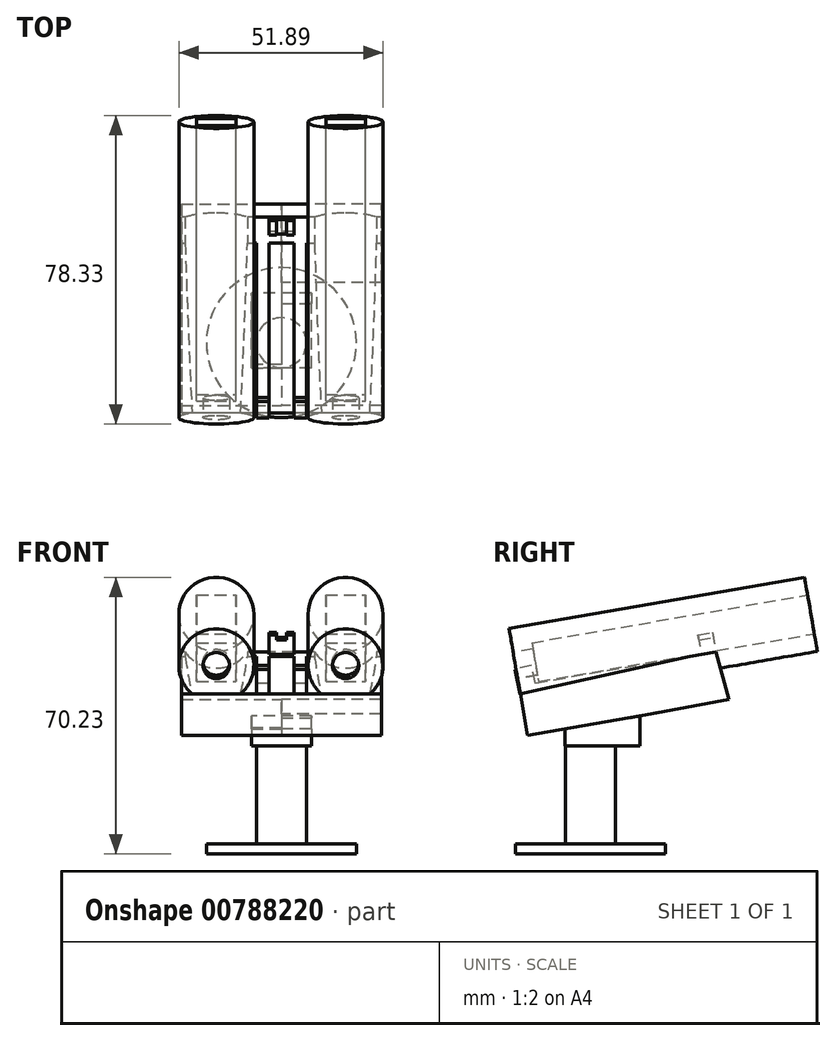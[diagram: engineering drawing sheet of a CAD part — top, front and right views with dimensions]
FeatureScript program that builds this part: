
annotation { "Feature Type Name" : "Feature", "Feature Type Description" : "" }
export const myFeature = defineFeature(function(context is Context, id is Id, definition is map)
    precondition{}
    {
        {
            var Q0;
            Q0=qCreatedBy(makeId("Top.planeOp"),FACE);
            var sketch = newSketch(context, id + "F0", { "sketchPlane" : qUnion([Q0])});
            skCircle(sketch, "E0", {"center": v(0, 0) * mm, "radius": 19.05 * mm});
            skSolve(sketch);
        }
        {
            var Q0;
            Q0 = qSketchRegion(id + "F0", true);
            extrude(context, id + "F1", {"entities" : qUnion([Q0]), "depth" : 2.54 * mm, "offsetDistance" : 25.4 * mm});
        }
        {
            var Q0;
            Q0=makeQuery(id+"F1.opExtrude","CAP_FACE",FACE,{"disambiguationData":[OSD([sQuery(id+"F0.wireOp",EDGE,"E0")])],"isStart":false});
            var sketch = newSketch(context, id + "F2", { "sketchPlane" : qUnion([Q0])});
            skCircle(sketch, "E1", {"center": v(0, 0) * mm, "radius": 6.35 * mm});
            skSolve(sketch);
        }
        {
            var Q0;
            Q0 = qSketchRegion(id + "F2", true);
            extrude(context, id + "F3", {"entities" : qUnion([Q0]), "operationType" : NewBodyOperationType.ADD, "depth" : 25.4 * mm, "offsetDistance" : 25.4 * mm});
        }
        {
            var Q0;
            Q0=qCreatedBy(makeId("Right.planeOp"),FACE);
            var sketch = newSketch(context, id + "F4", { "sketchPlane" : qUnion([Q0])});
            skLineSegment(sketch, "E2", {"start": v(-6.4, 27.4) * mm, "end": v(12.65, 27.4) * mm});
            skLineSegment(sketch, "E3", {"start": v(12.65, 27.4) * mm, "end": v(12.65, 35.02) * mm});
            skLineSegment(sketch, "E4", {"start": v(12.65, 35.02) * mm, "end": v(-6.4, 31.8) * mm});
            skLineSegment(sketch, "E5", {"start": v(-6.4, 31.8) * mm, "end": v(-6.4, 27.4) * mm});
            skSolve(sketch);
        }
        {
            var Q0;
            Q0 = qSketchRegion(id + "F4", true);
            extrude(context, id + "F5", {"entities" : qUnion([Q0]), "operationType" : NewBodyOperationType.ADD, "depth" : 7.62 * mm, "offsetDistance" : 25.4 * mm});
        }
        {
            var Q0;
            Q0=makeQuery(id+"F5.opExtrude","CAP_FACE",FACE,{"disambiguationData":[OSD([sQuery(id+"F4.wireOp",EDGE,"E2"),sQuery(id+"F4.wireOp",EDGE,"E3"),sQuery(id+"F4.wireOp",EDGE,"E4"),sQuery(id+"F4.wireOp",EDGE,"E5")])],"isStart":true});
            var sketch = newSketch(context, id + "F6", { "sketchPlane" : qUnion([Q0])});
            skLineSegment(sketch, "E6", {"start": v(-12.65, 27.4) * mm, "end": v(6.4, 27.4) * mm});
            skLineSegment(sketch, "E7", {"start": v(6.4, 27.4) * mm, "end": v(6.4, 31.8) * mm});
            skLineSegment(sketch, "E8", {"start": v(6.4, 31.8) * mm, "end": v(-12.65, 35.02) * mm});
            skLineSegment(sketch, "E9", {"start": v(-12.65, 35.02) * mm, "end": v(-12.65, 27.4) * mm});
            skSolve(sketch);
        }
        {
            var Q0;
            Q0 = qSketchRegion(id + "F6", true);
            extrude(context, id + "F7", {"entities" : qUnion([Q0]), "operationType" : NewBodyOperationType.ADD, "depth" : 7.62 * mm, "offsetDistance" : 25.4 * mm});
        }
        {
            var Q0;
            Q0=qCreatedBy(makeId("Right.planeOp"),FACE);
            var sketch = newSketch(context, id + "F8", { "sketchPlane" : qUnion([Q0])});
            skLineSegment(sketch, "E10", {"start": v(15.34, 35.5) * mm, "end": v(-15.94, 30.08) * mm});
            skLineSegment(sketch, "E11", {"start": v(-15.94, 30.08) * mm, "end": v(-18.11, 42.59) * mm});
            skLineSegment(sketch, "E12", {"start": v(-18.11, 42.59) * mm, "end": v(31.94, 51.26) * mm});
            skLineSegment(sketch, "E13", {"start": v(15.34, 35.5) * mm, "end": v(35.23, 39.24) * mm});
            skLineSegment(sketch, "E14", {"start": v(35.23, 39.24) * mm, "end": v(31.94, 51.26) * mm});
            skSolve(sketch);
        }
        {
            var Q0;
            Q0 = qSketchRegion(id + "F8", true);
            extrude(context, id + "F9", {"entities" : qUnion([Q0]), "operationType" : NewBodyOperationType.ADD, "depth" : 25.4 * mm, "offsetDistance" : 25.4 * mm});
        }
        {
            var Q0;
            Q0=makeQuery(id+"F9.opExtrude","CAP_FACE",FACE,{"disambiguationData":[OSD([sQuery(id+"F8.wireOp",EDGE,"E10"),sQuery(id+"F8.wireOp",EDGE,"E11"),sQuery(id+"F8.wireOp",EDGE,"E12"),sQuery(id+"F8.wireOp",EDGE,"E13"),sQuery(id+"F8.wireOp",EDGE,"E14")])],"isStart":true});
            var sketch = newSketch(context, id + "F10", { "sketchPlane" : qUnion([Q0])});
            skLineSegment(sketch, "E15", {"start": v(-35.23, 39.24) * mm, "end": v(15.94, 30.08) * mm});
            skLineSegment(sketch, "E16", {"start": v(15.94, 30.08) * mm, "end": v(18.11, 42.59) * mm});
            skLineSegment(sketch, "E17", {"start": v(18.11, 42.59) * mm, "end": v(-31.94, 51.26) * mm});
            skLineSegment(sketch, "E18", {"start": v(-31.94, 51.26) * mm, "end": v(-35.23, 39.24) * mm});
            skSolve(sketch);
        }
        {
            var Q0;
            Q0 = qSketchRegion(id + "F10", true);
            extrude(context, id + "F11", {"entities" : qUnion([Q0]), "operationType" : NewBodyOperationType.ADD, "depth" : 25.4 * mm, "offsetDistance" : 25.4 * mm});
        }
        {
            var Q0;
            Q0=qCreatedBy(makeId("Right.planeOp"),FACE);
            var sketch = newSketch(context, id + "F12", { "sketchPlane" : qUnion([Q0])});
            skLineSegment(sketch, "E19", {"start": v(-17.83, 40.68) * mm, "end": v(-19.2, 46.88) * mm});
            skLineSegment(sketch, "E20", {"start": v(-19.2, 46.88) * mm, "end": v(-14.9, 47.82) * mm});
            skLineSegment(sketch, "E21", {"start": v(-14.9, 47.82) * mm, "end": v(-13.34, 40.68) * mm});
            skLineSegment(sketch, "E22", {"start": v(-13.34, 40.68) * mm, "end": v(-17.83, 40.68) * mm});
            skSolve(sketch);
        }
        {
            var Q0;
            Q0 = qSketchRegion(id + "F12", true);
            extrude(context, id + "F13", {"entities" : qUnion([Q0]), "operationType" : NewBodyOperationType.ADD, "depth" : 25.4 * mm, "offsetDistance" : 25.4 * mm});
        }
        {
            var Q0;
            Q0=makeQuery(id+"F13.opExtrude","CAP_FACE",FACE,{"disambiguationData":[OSD([sQuery(id+"F12.wireOp",EDGE,"E19"),sQuery(id+"F12.wireOp",EDGE,"E20"),sQuery(id+"F12.wireOp",EDGE,"E21"),sQuery(id+"F12.wireOp",EDGE,"E22")])],"isStart":true});
            var sketch = newSketch(context, id + "F14", { "sketchPlane" : qUnion([Q0])});
            skLineSegment(sketch, "E23", {"start": v(17.83, 40.68) * mm, "end": v(19.2, 46.88) * mm});
            skLineSegment(sketch, "E24", {"start": v(19.2, 46.88) * mm, "end": v(14.9, 47.82) * mm});
            skLineSegment(sketch, "E25", {"start": v(14.9, 47.82) * mm, "end": v(13.34, 40.68) * mm});
            skLineSegment(sketch, "E26", {"start": v(13.34, 40.68) * mm, "end": v(17.83, 40.68) * mm});
            skSolve(sketch);
        }
        {
            var Q0;
            Q0 = qSketchRegion(id + "F14", true);
            extrude(context, id + "F15", {"entities" : qUnion([Q0]), "operationType" : NewBodyOperationType.ADD, "depth" : 25.4 * mm, "offsetDistance" : 25.4 * mm});
        }
        {
            var Q0;
            Q0=makeQuery(id+"F15.boolean.opBoolean","MERGE",FACE,{"derivedFrom":[makeQuery(id+"F13.opExtrude","SWEPT_FACE",FACE,{"disambiguationData":[OSD([sQuery(id+"F12.wireOp",EDGE,"E19")])]}),makeQuery(id+"F15.opExtrude","SWEPT_FACE",FACE,{"disambiguationData":[OSD([sQuery(id+"F14.wireOp",EDGE,"E23")])]})]});
            var sketch = newSketch(context, id + "F16", { "sketchPlane" : qUnion([Q0])});
            skLineSegment(sketch, "E27", {"start": v(-25.4, 49.9) * mm, "end": v(-6.35, 49.9) * mm});
            skLineSegment(sketch, "E28", {"start": v(-6.35, 49.9) * mm, "end": v(-6.35, 43.55) * mm});
            skLineSegment(sketch, "E29", {"start": v(-6.35, 43.55) * mm, "end": v(-25.4, 43.55) * mm});
            skLineSegment(sketch, "E30", {"start": v(-25.4, 43.55) * mm, "end": v(-25.4, 49.9) * mm});
            skSolve(sketch);
        }
        {
            var Q0;
            Q0 = qSketchRegion(id + "F16", true);
            extrude(context, id + "F17", {"entities" : qUnion([Q0]), "operationType" : NewBodyOperationType.REMOVE, "oppositeDirection" : true, "depth" : 50.8 * mm, "offsetDistance" : 25.4 * mm});
        }
        {
            var Q0;
            Q0=makeQuery(id+"F15.boolean.opBoolean","MERGE",FACE,{"derivedFrom":[makeQuery(id+"F13.opExtrude","SWEPT_FACE",FACE,{"disambiguationData":[OSD([sQuery(id+"F12.wireOp",EDGE,"E19")])]}),makeQuery(id+"F15.opExtrude","SWEPT_FACE",FACE,{"disambiguationData":[OSD([sQuery(id+"F14.wireOp",EDGE,"E23")])]})]});
            var sketch = newSketch(context, id + "F18", { "sketchPlane" : qUnion([Q0])});
            skLineSegment(sketch, "E31", {"start": v(25.4, 49.9) * mm, "end": v(6.35, 49.9) * mm});
            skLineSegment(sketch, "E32", {"start": v(6.35, 49.9) * mm, "end": v(6.35, 43.55) * mm});
            skPoint(sketch, "E32.endSnap0", {"position": v(9.53, 43.55) * mm});
            skLineSegment(sketch, "E33", {"start": v(6.35, 43.55) * mm, "end": v(25.4, 43.55) * mm});
            skLineSegment(sketch, "E34", {"start": v(25.4, 43.55) * mm, "end": v(25.4, 49.9) * mm});
            skSolve(sketch);
        }
        {
            var Q0;
            Q0 = qSketchRegion(id + "F18", true);
            extrude(context, id + "F19", {"entities" : qUnion([Q0]), "operationType" : NewBodyOperationType.REMOVE, "oppositeDirection" : true, "depth" : 50.8 * mm, "offsetDistance" : 25.4 * mm});
        }
        {
            var Q0;
            Q0=makeQuery(id+"F15.boolean.opBoolean","MERGE",FACE,{"derivedFrom":[makeQuery(id+"F13.opExtrude","SWEPT_FACE",FACE,{"disambiguationData":[OSD([sQuery(id+"F12.wireOp",EDGE,"E19")])]}),makeQuery(id+"F15.opExtrude","SWEPT_FACE",FACE,{"disambiguationData":[OSD([sQuery(id+"F14.wireOp",EDGE,"E23")])]})]});
            var sketch = newSketch(context, id + "F20", { "sketchPlane" : qUnion([Q0])});
            skLineSegment(sketch, "E35", {"start": v(0, 49.9) * mm, "end": v(-3.17, 49.9) * mm});
            skLineSegment(sketch, "E36", {"start": v(-3.17, 49.9) * mm, "end": v(-3.17, 43.55) * mm});
            skLineSegment(sketch, "E37", {"start": v(0, 49.9) * mm, "end": v(3.18, 49.9) * mm});
            skLineSegment(sketch, "E38", {"start": v(3.18, 49.9) * mm, "end": v(3.18, 43.55) * mm});
            skLineSegment(sketch, "E39", {"start": v(3.17, 43.55) * mm, "end": v(-3.17, 43.55) * mm});
            skSolve(sketch);
        }
        {
            var Q0;
            Q0 = qSketchRegion(id + "F20", true);
            extrude(context, id + "F21", {"entities" : qUnion([Q0]), "operationType" : NewBodyOperationType.REMOVE, "oppositeDirection" : true, "depth" : 50.8 * mm, "offsetDistance" : 25.4 * mm});
        }
        {
            var Q0;
            Q0=makeQuery(id+"F11.boolean.opBoolean","MERGE",FACE,{"derivedFrom":[makeQuery(id+"F9.opExtrude","SWEPT_FACE",FACE,{"disambiguationData":[OSD([sQuery(id+"F8.wireOp",EDGE,"E12")])]}),makeQuery(id+"F11.opExtrude","SWEPT_FACE",FACE,{"disambiguationData":[OSD([sQuery(id+"F10.wireOp",EDGE,"E17")])]})]});
            var sketch = newSketch(context, id + "F22", { "sketchPlane" : qUnion([Q0])});
            skLineSegment(sketch, "E40", {"start": v(0, 40.23) * mm, "end": v(3.18, 40.23) * mm});
            skLineSegment(sketch, "E41", {"start": v(3.18, 40.23) * mm, "end": v(3.18, 36.42) * mm});
            skLineSegment(sketch, "E42", {"start": v(3.18, 36.42) * mm, "end": v(-3.17, 36.42) * mm});
            skLineSegment(sketch, "E43", {"start": v(-3.17, 36.42) * mm, "end": v(-3.17, 40.23) * mm});
            skLineSegment(sketch, "E44", {"start": v(-3.17, 40.23) * mm, "end": v(0, 40.23) * mm});
            skSolve(sketch);
        }
        {
            var Q0;
            Q0 = qSketchRegion(id + "F22", true);
            extrude(context, id + "F23", {"entities" : qUnion([Q0]), "operationType" : NewBodyOperationType.ADD, "depth" : 5.08 * mm, "offsetDistance" : 25.4 * mm});
        }
        {
            var Q0;
            Q0=makeQuery(id+"F23.opExtrude","SWEPT_FACE",FACE,{"disambiguationData":[OSD([sQuery(id+"F22.wireOp",EDGE,"E40"),sQuery(id+"F22.wireOp",EDGE,"E44")])]});
            var sketch = newSketch(context, id + "F24", { "sketchPlane" : qUnion([Q0])});
            skLineSegment(sketch, "E45", {"start": v(0, 50.14) * mm, "end": v(-1.27, 50.14) * mm});
            skLineSegment(sketch, "E46", {"start": v(0, 50.14) * mm, "end": v(1.27, 50.14) * mm});
            skLineSegment(sketch, "E47", {"start": v(1.27, 50.14) * mm, "end": v(1.27, 48.87) * mm});
            skLineSegment(sketch, "E48", {"start": v(1.27, 48.87) * mm, "end": v(-1.27, 48.87) * mm});
            skLineSegment(sketch, "E49", {"start": v(-1.27, 48.87) * mm, "end": v(-1.27, 50.14) * mm});
            skSolve(sketch);
        }
        {
            var Q0;
            Q0 = qSketchRegion(id + "F24", true);
            extrude(context, id + "F25", {"entities" : qUnion([Q0]), "operationType" : NewBodyOperationType.REMOVE, "oppositeDirection" : true, "depth" : 25.4 * mm, "offsetDistance" : 25.4 * mm});
        }
        {
            var Q0;
            Q0=makeQuery(id+"F11.boolean.opBoolean","MERGE",FACE,{"derivedFrom":[makeQuery(id+"F9.opExtrude","SWEPT_FACE",FACE,{"disambiguationData":[OSD([sQuery(id+"F8.wireOp",EDGE,"E11")])]}),makeQuery(id+"F11.opExtrude","SWEPT_FACE",FACE,{"disambiguationData":[OSD([sQuery(id+"F10.wireOp",EDGE,"E16")])]})]});
            var sketch = newSketch(context, id + "F26", { "sketchPlane" : qUnion([Q0])});
            skCircle(sketch, "E50", {"center": v(-16.52, 50.38) * mm, "radius": 9.53 * mm});
            skCircle(sketch, "E51", {"center": v(16.33, 50.38) * mm, "radius": 9.53 * mm});
            skSolve(sketch);
        }
        {
            var Q0;
            Q0 = qSketchRegion(id + "F26", true);
            extrude(context, id + "F27", {"entities" : qUnion([Q0]), "operationType" : NewBodyOperationType.ADD, "oppositeDirection" : true, "depth" : 76.2 * mm, "offsetDistance" : 25.4 * mm});
        }
        {
            var Q0;
            Q0=makeQuery(id+"F27.opExtrude","CAP_FACE",FACE,{"disambiguationData":[OSD([sQuery(id+"F26.wireOp",EDGE,"E51")])],"isStart":false});
            var sketch = newSketch(context, id + "F28", { "sketchPlane" : qUnion([Q0])});
            skLineSegment(sketch, "E52.bottom", {"start": v(-11.33, 55.38) * mm, "end": v(-21.33, 55.38) * mm});
            skLineSegment(sketch, "E52.top", {"start": v(-11.33, 45.38) * mm, "end": v(-21.33, 45.38) * mm});
            skLineSegment(sketch, "E52.left", {"start": v(-11.33, 55.38) * mm, "end": v(-11.33, 45.38) * mm});
            skLineSegment(sketch, "E52.right", {"start": v(-21.33, 55.38) * mm, "end": v(-21.33, 45.38) * mm});
            skPoint(sketch, "E52.middle", {"position": v(-16.33, 50.38) * mm});
            skSolve(sketch);
        }
        {
            var Q0;
            Q0=makeQuery(id+"F27.opExtrude","CAP_FACE",FACE,{"disambiguationData":[OSD([sQuery(id+"F26.wireOp",EDGE,"E50")])],"isStart":false});
            var sketch = newSketch(context, id + "F29", { "sketchPlane" : qUnion([Q0])});
            skLineSegment(sketch, "E53.bottom", {"start": v(21.52, 55.38) * mm, "end": v(11.52, 55.38) * mm});
            skLineSegment(sketch, "E53.top", {"start": v(21.52, 45.38) * mm, "end": v(11.52, 45.38) * mm});
            skLineSegment(sketch, "E53.left", {"start": v(21.52, 55.38) * mm, "end": v(21.52, 45.38) * mm});
            skLineSegment(sketch, "E53.right", {"start": v(11.52, 55.38) * mm, "end": v(11.52, 45.38) * mm});
            skPoint(sketch, "E53.middle", {"position": v(16.52, 50.38) * mm});
            skSolve(sketch);
        }
        {
            var Q0;
            Q0 = qSketchRegion(id + "F29", true);
            extrude(context, id + "F30", {"entities" : qUnion([Q0]), "operationType" : NewBodyOperationType.REMOVE, "oppositeDirection" : true, "depth" : 71.12 * mm, "offsetDistance" : 25.4 * mm});
        }
        {
            var Q0;
            Q0=makeQuery(id+"F28.imprint","IMPRINT",FACE,{"disambiguationData":[TD([[makeQuery(id+"F28.imprint","IMPRINT",EDGE,{"derivedFrom":sQuery(id+"F28.wireOp",EDGE,"E52.bottom")}),1.0]])]});
            extrude(context, id + "F31", {"entities" : qUnion([Q0]), "operationType" : NewBodyOperationType.REMOVE, "oppositeDirection" : true, "depth" : 71.12 * mm, "offsetDistance" : 25.4 * mm});
        }
        {
            var Q0;
            Q0=makeQuery(id+"F27.opExtrude","CAP_FACE",FACE,{"disambiguationData":[OSD([sQuery(id+"F26.wireOp",EDGE,"E50")])],"isStart":true});
            var sketch = newSketch(context, id + "F32", { "sketchPlane" : qUnion([Q0])});
            skCircle(sketch, "E54", {"center": v(-16.52, 50.38) * mm, "radius": 3.37 * mm});
            skSolve(sketch);
        }
        {
            var Q0;
            Q0=makeQuery(id+"F27.opExtrude","CAP_FACE",FACE,{"disambiguationData":[OSD([sQuery(id+"F26.wireOp",EDGE,"E51")])],"isStart":true});
            var sketch = newSketch(context, id + "F33", { "sketchPlane" : qUnion([Q0])});
            skCircle(sketch, "E55", {"center": v(16.33, 50.38) * mm, "radius": 3.37 * mm});
            skSolve(sketch);
        }
        {
            var Q0;
            Q0=makeQuery(id+"F33.imprint","IMPRINT",FACE,{"disambiguationData":[TD([[makeQuery(id+"F33.imprint","IMPRINT",EDGE,{"derivedFrom":sQuery(id+"F33.wireOp",EDGE,"E55")}),1.0]])]});
            var Q1;
            Q1=makeQuery(id+"F32.imprint","IMPRINT",FACE,{"disambiguationData":[TD([[makeQuery(id+"F32.imprint","IMPRINT",EDGE,{"derivedFrom":sQuery(id+"F32.wireOp",EDGE,"E54")}),1.0]])]});
            var Q2;
            Q2=sQuery(id+"F32.wireOp",EDGE,"E54");
            var Q3;
            Q3=sQuery(id+"F33.wireOp",EDGE,"E55");
            extrude(context, id + "F34", {"entities" : qUnion([Q0, Q1]), "operationType" : NewBodyOperationType.REMOVE, "surfaceEntities" : qUnion([Q2, Q3]), "oppositeDirection" : true, "depth" : 25.4 * mm, "offsetDistance" : 25.4 * mm});
        }
    });
